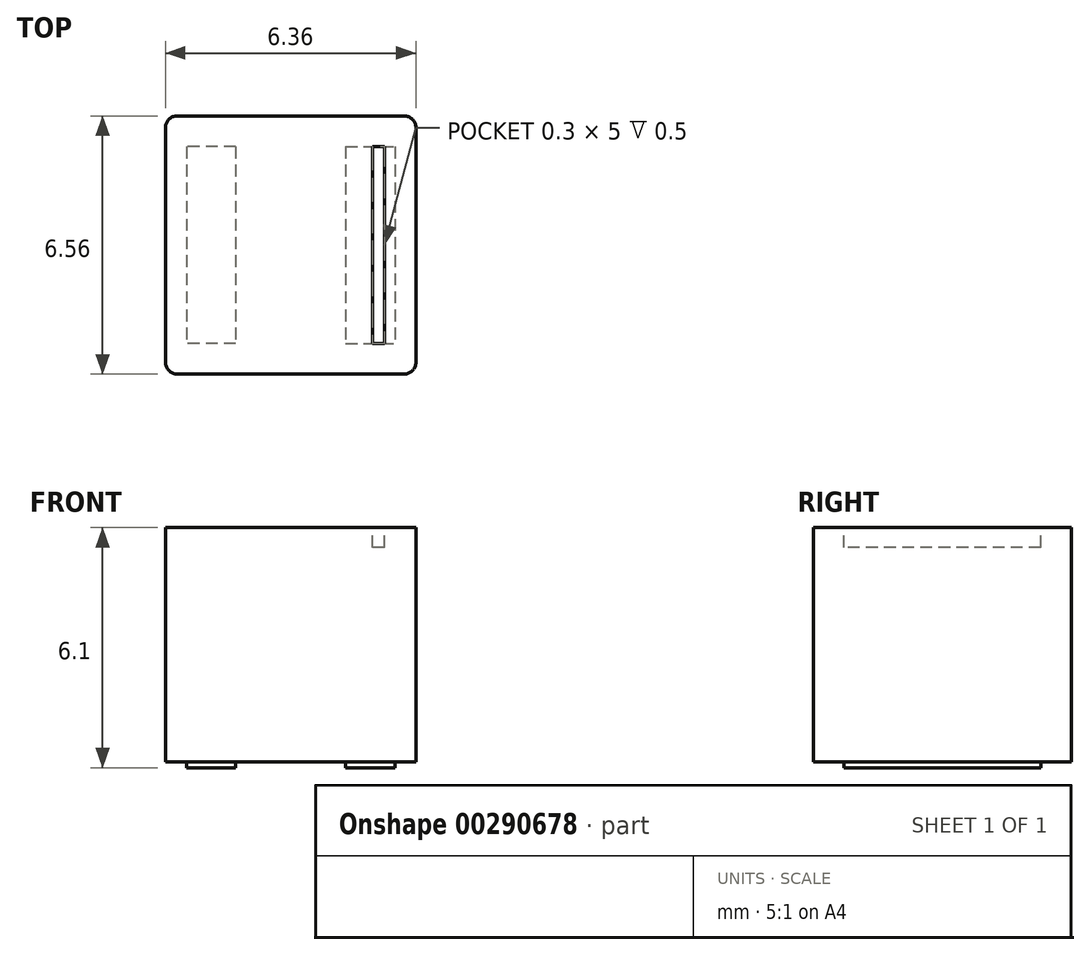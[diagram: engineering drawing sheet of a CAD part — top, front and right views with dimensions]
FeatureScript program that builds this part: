
annotation { "Feature Type Name" : "Feature", "Feature Type Description" : "" }
export const myFeature = defineFeature(function(context is Context, id is Id, definition is map)
    precondition{}
    {
        {
            var Q0;
            Q0=qCreatedBy(makeId("Top.planeOp"),FACE);
            var sketch = newSketch(context, id + "F0", { "sketchPlane" : qUnion([Q0])});
            skLineSegment(sketch, "E0.bottom", {"start": v(-1.4, 2.5) * mm, "end": v(-2.64, 2.5) * mm});
            skLineSegment(sketch, "E0.top", {"start": v(-1.4, -2.5) * mm, "end": v(-2.64, -2.5) * mm});
            skLineSegment(sketch, "E0.left", {"start": v(-1.4, 2.5) * mm, "end": v(-1.4, -2.5) * mm});
            skLineSegment(sketch, "E0.right", {"start": v(-2.64, 2.5) * mm, "end": v(-2.64, -2.5) * mm});
            skLineSegment(sketch, "E1.bottom", {"start": v(1.4, 2.5) * mm, "end": v(2.65, 2.5) * mm});
            skLineSegment(sketch, "E1.top", {"start": v(1.4, -2.5) * mm, "end": v(2.65, -2.5) * mm});
            skLineSegment(sketch, "E1.left", {"start": v(1.4, 2.5) * mm, "end": v(1.4, -2.5) * mm});
            skLineSegment(sketch, "E1.right", {"start": v(2.65, 2.5) * mm, "end": v(2.65, -2.5) * mm});
            skLineSegment(sketch, "E2", {"start": v(-1.4, 2.5) * mm, "end": v(0, 0) * mm, "construction": true});
            skLineSegment(sketch, "E3", {"start": v(0, 0) * mm, "end": v(-1.4, -2.5) * mm, "construction": true});
            skLineSegment(sketch, "E4", {"start": v(0, 0) * mm, "end": v(1.4, -2.5) * mm, "construction": true});
            skLineSegment(sketch, "E5", {"start": v(0, 0) * mm, "end": v(1.4, 2.5) * mm, "construction": true});
            skSolve(sketch);
        }
        {
            var Q0;
            Q0 = qSketchRegion(id + "F0", true);
            extrude(context, id + "F1", {"entities" : qUnion([Q0]), "depth" : .15 * mm});
        }
        {
            var Q0;
            Q0=makeQuery(id+"F1.opExtrude","CAP_FACE",FACE,{"disambiguationData":[OSD([sQuery(id+"F0.wireOp",EDGE,"E0.bottom"),sQuery(id+"F0.wireOp",EDGE,"E0.top"),sQuery(id+"F0.wireOp",EDGE,"E0.left"),sQuery(id+"F0.wireOp",EDGE,"E0.right")])],"isStart":false});
            var sketch = newSketch(context, id + "F2", { "sketchPlane" : qUnion([Q0])});
            skLineSegment(sketch, "E6.bottom", {"start": v(-3.18, 3.28) * mm, "end": v(3.18, 3.28) * mm});
            skLineSegment(sketch, "E6.top", {"start": v(-3.18, -3.28) * mm, "end": v(3.18, -3.28) * mm});
            skLineSegment(sketch, "E6.left", {"start": v(-3.18, 3.28) * mm, "end": v(-3.18, -3.28) * mm});
            skLineSegment(sketch, "E6.right", {"start": v(3.18, 3.28) * mm, "end": v(3.18, -3.28) * mm});
            skLineSegment(sketch, "E7", {"start": v(-3.18, 3.28) * mm, "end": v(0, 0) * mm, "construction": true});
            skLineSegment(sketch, "E8", {"start": v(0, 0) * mm, "end": v(3.18, 3.28) * mm, "construction": true});
            skLineSegment(sketch, "E9", {"start": v(0, 0) * mm, "end": v(3.18, -3.28) * mm, "construction": true});
            skLineSegment(sketch, "E10", {"start": v(0, 0) * mm, "end": v(-3.18, -3.28) * mm, "construction": true});
            skSolve(sketch);
        }
        {
            var Q0;
            Q0 = qSketchRegion(id + "F2", true);
            extrude(context, id + "F3", {"entities" : qUnion([Q0]), "depth" : (6.1 - .15) * mm});
        }
        {
            var Q0;
            Q0=makeQuery(id+"F3.opExtrude","CAP_FACE",FACE,{"disambiguationData":[OSD([sQuery(id+"F2.wireOp",EDGE,"E6.bottom"),sQuery(id+"F2.wireOp",EDGE,"E6.top"),sQuery(id+"F2.wireOp",EDGE,"E6.left"),sQuery(id+"F2.wireOp",EDGE,"E6.right")])],"isStart":false});
            var sketch = newSketch(context, id + "F4", { "sketchPlane" : qUnion([Q0])});
            skLineSegment(sketch, "E11.bottom", {"start": v(2.38, 2.5) * mm, "end": v(2.08, 2.5) * mm});
            skLineSegment(sketch, "E11.top", {"start": v(2.38, -2.5) * mm, "end": v(2.08, -2.5) * mm});
            skLineSegment(sketch, "E11.left", {"start": v(2.38, 2.5) * mm, "end": v(2.38, -2.5) * mm});
            skLineSegment(sketch, "E11.right", {"start": v(2.08, 2.5) * mm, "end": v(2.08, -2.5) * mm});
            skLineSegment(sketch, "E12", {"start": v(2.38, 2.5) * mm, "end": v(3.18, 3.28) * mm, "construction": true});
            skLineSegment(sketch, "E13", {"start": v(2.38, -2.5) * mm, "end": v(3.18, -3.28) * mm, "construction": true});
            skSolve(sketch);
        }
        {
            var Q0;
            Q0 = qSketchRegion(id + "F4", true);
            extrude(context, id + "F5", {"entities" : qUnion([Q0]), "operationType" : NewBodyOperationType.REMOVE, "oppositeDirection" : true, "depth" : .5 * mm});
        }
        {
            var Q0;
            Q0=makeQuery(id+"F3.opExtrude","SWEPT_EDGE",EDGE,{"disambiguationData":[OSD([sQuery(id+"F2.wireOp",EDGE,"E6.top"),sQuery(id+"F2.wireOp",EDGE,"E6.right")])]});
            var Q1;
            Q1=makeQuery(id+"F3.opExtrude","SWEPT_EDGE",EDGE,{"disambiguationData":[OSD([sQuery(id+"F2.wireOp",EDGE,"E6.bottom"),sQuery(id+"F2.wireOp",EDGE,"E6.right")])]});
            var Q2;
            Q2=makeQuery(id+"F3.opExtrude","SWEPT_EDGE",EDGE,{"disambiguationData":[OSD([sQuery(id+"F2.wireOp",EDGE,"E6.top"),sQuery(id+"F2.wireOp",EDGE,"E6.left")])]});
            var Q3;
            Q3=makeQuery(id+"F3.opExtrude","SWEPT_EDGE",EDGE,{"disambiguationData":[OSD([sQuery(id+"F2.wireOp",EDGE,"E6.bottom"),sQuery(id+"F2.wireOp",EDGE,"E6.left")])]});
            fillet(context, id + "F6", {"entities" : qUnion([Q0, Q1, Q2, Q3]), "radius" : .3 * mm, "tangentPropagation" : true, "allowEdgeOverflow" : false});
        }
    });
